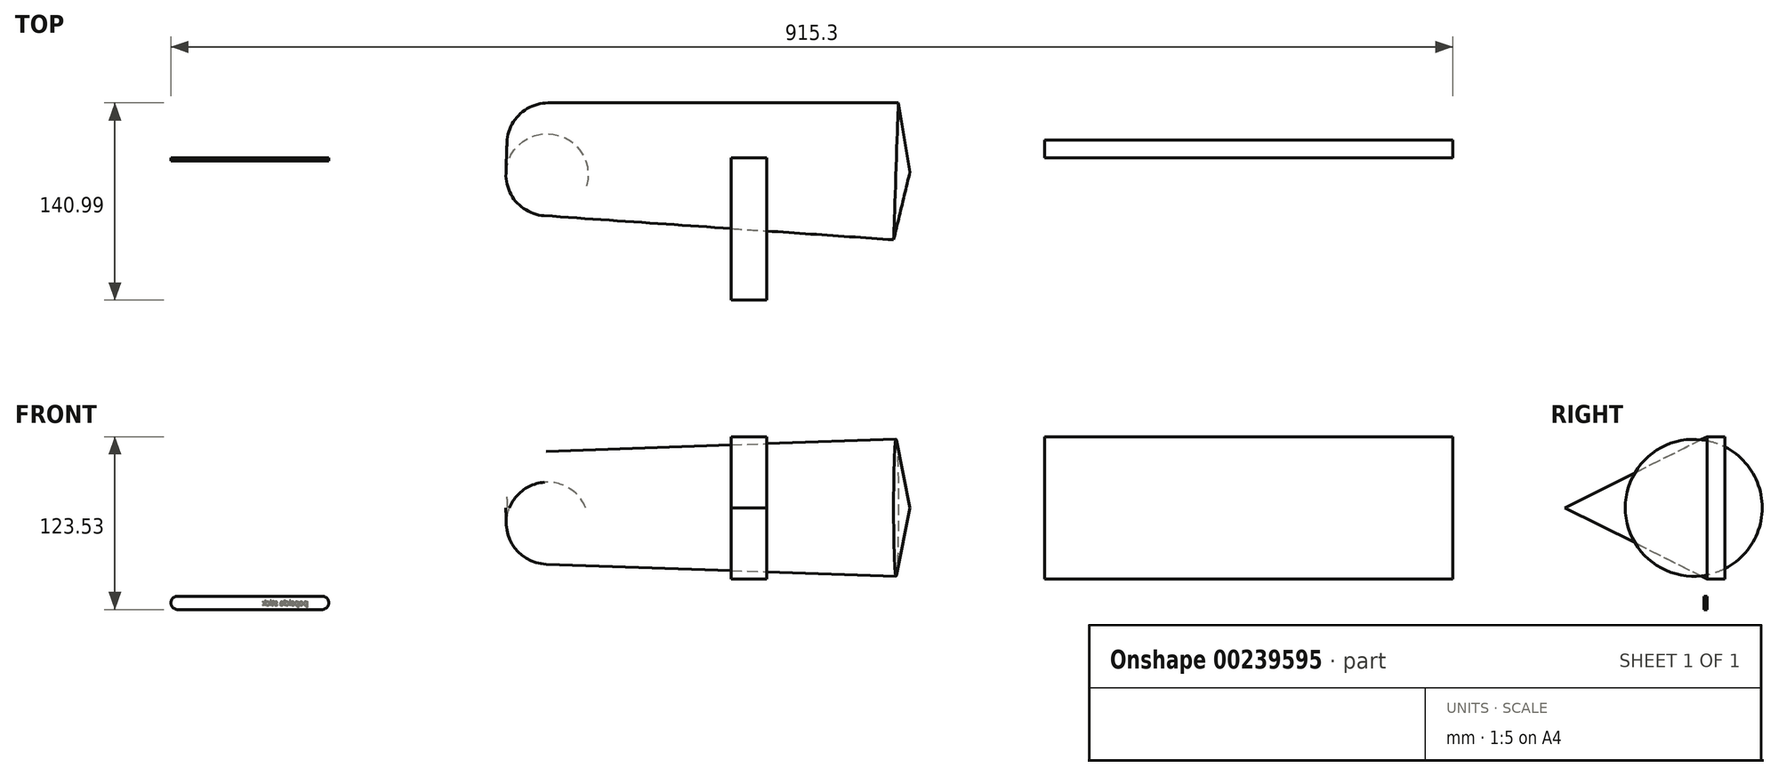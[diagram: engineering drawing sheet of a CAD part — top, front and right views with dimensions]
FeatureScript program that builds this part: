
annotation { "Feature Type Name" : "Feature", "Feature Type Description" : "" }
export const myFeature = defineFeature(function(context is Context, id is Id, definition is map)
    precondition{}
    {
        {
            var Q0;
            Q0=qCreatedBy(makeId("Top.planeOp"),FACE);
            var sketch = newSketch(context, id + "F0", { "sketchPlane" : qUnion([Q0])});
            skLineSegment(sketch, "E0", {"start": v(-130.74, 39.4) * mm, "end": v(119.37, 39.4) * mm});
            skLineSegment(sketch, "E1", {"start": v(119.37, 39.4) * mm, "end": v(127.7, -9.85) * mm});
            skArc(sketch, "E2", {"start": v(-130.74, 39.4) * mm, "mid": v(-154.78, 26.87) * mm, "end": v(-158.3, 0) * mm});
            skLineSegment(sketch, "E3", {"start": v(-158.3, 0) * mm, "end": v(127.7, -9.85) * mm, "construction": true});
            skLineSegment(sketch, "E4", {"start": v(-158.3, 0) * mm, "end": v(127.7, -9.85) * mm});
            skSolve(sketch);
        }
        {
            var Q0;
            Q0 = qSketchRegion(id + "F0", true);
            var Q1;
            Q1=sQuery(id+"F0.wireOp",EDGE,"E4");
            revolve(context, id + "F1", {"entities" : qUnion([Q0]), "axis" : qUnion([Q1]), "revolveType" : RevolveType.FULL});
        }
        {
            var Q0;
            Q0=qCreatedBy(makeId("Front.planeOp"),FACE);
            var sketch = newSketch(context, id + "F2", { "sketchPlane" : qUnion([Q0])});
            skLineSegment(sketch, "E5", {"start": v(-292.09, -63.2) * mm, "end": v(-395.28, -63.2) * mm});
            skArc(sketch, "E6", {"start": v(-395.28, -63.2) * mm, "mid": v(-400.04, -67.96) * mm, "end": v(-395.28, -72.73) * mm});
            skLineSegment(sketch, "E7", {"start": v(-395.28, -72.73) * mm, "end": v(-292.09, -72.73) * mm});
            skArc(sketch, "E8", {"start": v(-292.09, -72.73) * mm, "mid": v(-287.33, -67.96) * mm, "end": v(-292.09, -63.2) * mm});
            skLineSegment(sketch, "E9", {"start": v(-292.09, -72.73) * mm, "end": v(-292.09, -63.2) * mm});
            skLineSegment(sketch, "E10", {"start": v(-395.28, -63.2) * mm, "end": v(-395.28, -72.73) * mm});
            skSolve(sketch);
        }
        {
            var Q0;
            Q0 = qSketchRegion(id + "F2", true);
            extrude(context, id + "F3", {"entities" : qUnion([Q0]), "depth" : 2.03 * mm});
        }
        {
            var Q0;
            Q0=makeQuery(id+"F3.opExtrude","CAP_FACE",FACE,{"disambiguationData":[OSD([sQuery(id+"F2.wireOp",EDGE,"E5"),sQuery(id+"F2.wireOp",EDGE,"E6"),sQuery(id+"F2.wireOp",EDGE,"E7"),sQuery(id+"F2.wireOp",EDGE,"E8")])],"isStart":true});
            var sketch = newSketch(context, id + "F4", { "sketchPlane" : qUnion([Q0])});
            skText(sketch, "E11", { "text": "popsicle stick", "fontName": "OpenSans-Regular.ttf"});
            const initialGuessF4  = {"E11": [0.30223, -0.06985, 1, 0, 0.00377]};
            skSetInitialGuess(sketch, initialGuessF4);
            skSolve(sketch);
        }
        {
            var Q0;
            Q0 = qSketchRegion(id + "F4", true);
            extrude(context, id + "F5", {"entities" : qUnion([Q0]), "operationType" : NewBodyOperationType.REMOVE, "oppositeDirection" : true, "depth" : 0.25 * mm, "hasDraft" : true, "draftAngle" : 18 * degree});
        }
        {
            var Q0;
            Q0=qCreatedBy(makeId("Front.planeOp"),FACE);
            var sketch = newSketch(context, id + "F6", { "sketchPlane" : qUnion([Q0])});
            skLineSegment(sketch, "E12.bottom", {"start": v(223.75, 50.8) * mm, "end": v(515.26, 50.8) * mm});
            skLineSegment(sketch, "E12.top", {"start": v(223.75, -50.8) * mm, "end": v(515.26, -50.8) * mm});
            skLineSegment(sketch, "E12.left", {"start": v(223.75, 50.8) * mm, "end": v(223.75, -50.8) * mm});
            skLineSegment(sketch, "E12.right", {"start": v(515.26, 50.8) * mm, "end": v(515.26, -50.8) * mm});
            skPoint(sketch, "E12.middle", {"position": v(369.5, 0) * mm});
            skPoint(sketch, "E13", {"position": v(515.26, 0) * mm});
            skSolve(sketch);
        }
        {
            var Q0;
            Q0=qCreatedBy(makeId("Right.planeOp"),FACE);
            var sketch = newSketch(context, id + "F7", { "sketchPlane" : qUnion([Q0])});
            skLineSegment(sketch, "E14", {"start": v(0, 0) * mm, "end": v(-101.6, 0) * mm});
            skPoint(sketch, "E15.0", {"position": v(0, 50.8) * mm});
            skPoint(sketch, "E16.0", {"position": v(0, -50.8) * mm});
            skLineSegment(sketch, "E17", {"start": v(-101.6, 0) * mm, "end": v(0, 50.8) * mm});
            skLineSegment(sketch, "E18", {"start": v(-101.6, 0) * mm, "end": v(0, -50.8) * mm});
            skLineSegment(sketch, "E19", {"start": v(0, 50.8) * mm, "end": v(0, -50.8) * mm});
            skSolve(sketch);
        }
        {
            var Q0;
            Q0 = qSketchRegion(id + "F6", true);
            extrude(context, id + "F8", {"entities" : qUnion([Q0]), "oppositeDirection" : true, "depth" : 12.83 * mm});
        }
        {
            var Q0;
            Q0 = qSketchRegion(id + "F7", true);
            extrude(context, id + "F9", {"entities" : qUnion([Q0]), "depth" : 25.4 * mm});
        }
    });
